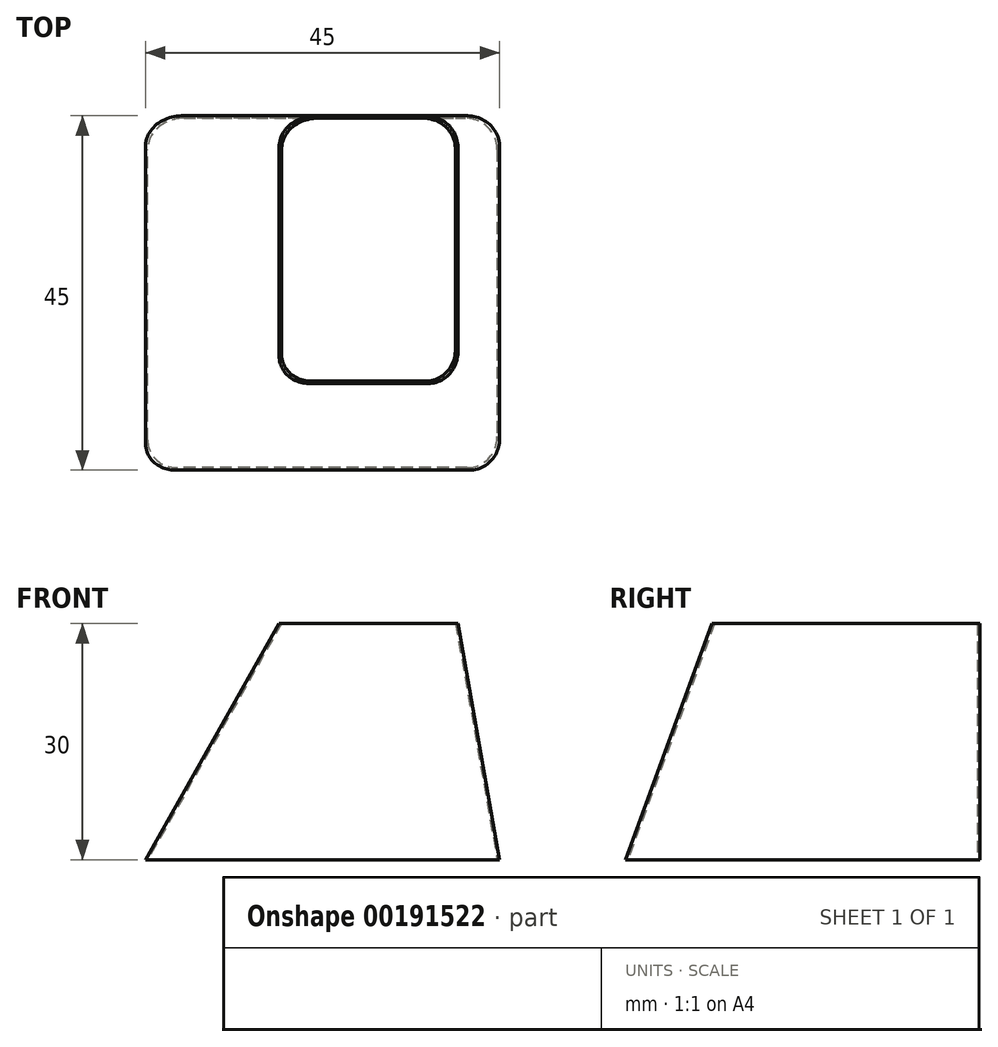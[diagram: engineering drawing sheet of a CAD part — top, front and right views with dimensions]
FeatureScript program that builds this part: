
annotation { "Feature Type Name" : "Feature", "Feature Type Description" : "" }
export const myFeature = defineFeature(function(context is Context, id is Id, definition is map)
    precondition{}
    {
        {
            var Q0;
            Q0=qCreatedBy(makeId("Top.planeOp"),FACE);
            var sketch = newSketch(context, id + "F0", { "sketchPlane" : qUnion([Q0])});
            skLineSegment(sketch, "E0.bottom", {"start": v(0, 0) * mm, "end": v(-45, 0) * mm});
            skLineSegment(sketch, "E0.top", {"start": v(0, 45) * mm, "end": v(-45, 45) * mm});
            skLineSegment(sketch, "E0.left", {"start": v(0, 0) * mm, "end": v(0, 45) * mm});
            skLineSegment(sketch, "E0.right", {"start": v(-45, 0) * mm, "end": v(-45, 45) * mm});
            skSolve(sketch);
        }
        {
            var Q0;
            Q0=qCreatedBy(makeId("Top.planeOp"),FACE);
            cPlane(context, id + "F1", {"entities" : qUnion([Q0]), "cplaneType" : CPlaneType.OFFSET, "offset" : 30 * mm, "width" : 150 * mm, "height" : 150 * mm});
        }
        {
            var Q0;
            Q0=qCreatedBy(id+"F1.planeOp",FACE);
            var sketch = newSketch(context, id + "F2", { "sketchPlane" : qUnion([Q0])});
            skLineSegment(sketch, "E1", {"start": v(0, 0) * mm, "end": v(-5.3, 0) * mm, "construction": true});
            skLineSegment(sketch, "E2", {"start": v(-5.3, 0) * mm, "end": v(-5.3, 11) * mm, "construction": true});
            skLineSegment(sketch, "E3.bottom", {"start": v(-5.3, 11) * mm, "end": v(-28, 11) * mm});
            skLineSegment(sketch, "E3.top", {"start": v(-5.3, 45) * mm, "end": v(-28, 45) * mm});
            skLineSegment(sketch, "E3.left", {"start": v(-5.3, 11) * mm, "end": v(-5.3, 45) * mm});
            skLineSegment(sketch, "E3.right", {"start": v(-28, 11) * mm, "end": v(-28, 45) * mm});
            skSolve(sketch);
        }
        {
            var Q0;
            Q0=makeQuery(id+"F2.imprint","IMPRINT",FACE,{"disambiguationData":[TD([[makeQuery(id+"F2.imprint","IMPRINT",EDGE,{"derivedFrom":sQuery(id+"F2.wireOp",EDGE,"E3.bottom")}),-1.0]])]});
            var Q1;
            Q1=makeQuery(id+"F0.imprint","IMPRINT",FACE,{"disambiguationData":[TD([[makeQuery(id+"F0.imprint","IMPRINT",EDGE,{"derivedFrom":sQuery(id+"F0.wireOp",EDGE,"E0.bottom")}),-1.0]])]});
            loft(context, id + "F3", {"sheetProfilesArray" : [{ "sheetProfileEntities" : qUnion([Q0]) }, { "sheetProfileEntities" : qUnion([Q1]) }]});
        }
        {
            var Q0;
            Q0=makeQuery(id+"F3.opLoft","CAP_FACE",FACE,{"disambiguationData":[OSD([makeQuery(id+"F2.imprint","IMPRINT",FACE,{"disambiguationData":[TD([[makeQuery(id+"F2.imprint","IMPRINT",EDGE,{"derivedFrom":sQuery(id+"F2.wireOp",EDGE,"E3.bottom")}),-1.0]])]})])],"isStart":true});
            var sketch = newSketch(context, id + "F4", { "sketchPlane" : qUnion([Q0])});
            skLineSegment(sketch, "E4.0", {"start": v(-27.7, 11.3) * mm, "end": v(-27.7, 44.7) * mm});
            skLineSegment(sketch, "E4.1", {"start": v(-5.6, 11.3) * mm, "end": v(-27.7, 11.3) * mm});
            skLineSegment(sketch, "E4.2", {"start": v(-5.6, 44.7) * mm, "end": v(-5.6, 11.3) * mm});
            skLineSegment(sketch, "E4.3", {"start": v(-27.7, 44.7) * mm, "end": v(-5.6, 44.7) * mm});
            skSolve(sketch);
        }
        {
            var Q0;
            Q0=makeQuery(id+"F3.opLoft","CAP_FACE",FACE,{"disambiguationData":[OSD([makeQuery(id+"F0.imprint","IMPRINT",FACE,{"disambiguationData":[TD([[makeQuery(id+"F0.imprint","IMPRINT",EDGE,{"derivedFrom":sQuery(id+"F0.wireOp",EDGE,"E0.bottom")}),-1.0]])]})])],"isStart":true});
            var sketch = newSketch(context, id + "F5", { "sketchPlane" : qUnion([Q0])});
            skLineSegment(sketch, "E5.0", {"start": v(-44.7, -0.3) * mm, "end": v(-44.7, -44.7) * mm});
            skLineSegment(sketch, "E5.1", {"start": v(-0.3, -0.3) * mm, "end": v(-44.7, -0.3) * mm});
            skLineSegment(sketch, "E5.2", {"start": v(-0.3, -44.7) * mm, "end": v(-0.3, -0.3) * mm});
            skLineSegment(sketch, "E5.3", {"start": v(-44.7, -44.7) * mm, "end": v(-0.3, -44.7) * mm});
            skSolve(sketch);
        }
        {
            var Q1;
            Q1 = qSketchRegion(id + "F4", true);
            var Q2;
            Q2 = qSketchRegion(id + "F5", true);
            loft(context, id + "F6", {"operationType" : NewBodyOperationType.REMOVE, "sheetProfilesArray" : [{ "sheetProfileEntities" : qUnion([Q1]) }, { "sheetProfileEntities" : qUnion([Q2]) }]});
        }
        {
            var Q0;
            Q0=makeQuery(id+"F6.boolean.opBoolean","COPY",EDGE,{"derivedFrom":makeQuery(id+"F6.opLoft","SWEPT_EDGE",EDGE,{"disambiguationData":[OSD([sQuery(id+"F4.wireOp",EDGE,"E4.0"),sQuery(id+"F4.wireOp",EDGE,"E4.3"),sQuery(id+"F5.wireOp",EDGE,"E5.0"),sQuery(id+"F5.wireOp",EDGE,"E5.3")])]})});
            var Q1;
            Q1=makeQuery(id+"F6.boolean.opBoolean","COPY",EDGE,{"derivedFrom":makeQuery(id+"F6.opLoft","SWEPT_EDGE",EDGE,{"disambiguationData":[OSD([sQuery(id+"F4.wireOp",EDGE,"E4.0"),sQuery(id+"F4.wireOp",EDGE,"E4.1"),sQuery(id+"F5.wireOp",EDGE,"E5.0"),sQuery(id+"F5.wireOp",EDGE,"E5.1")])]})});
            var Q2;
            Q2=makeQuery(id+"F6.boolean.opBoolean","COPY",EDGE,{"derivedFrom":makeQuery(id+"F6.opLoft","SWEPT_EDGE",EDGE,{"disambiguationData":[OSD([sQuery(id+"F4.wireOp",EDGE,"E4.1"),sQuery(id+"F4.wireOp",EDGE,"E4.2"),sQuery(id+"F5.wireOp",EDGE,"E5.1"),sQuery(id+"F5.wireOp",EDGE,"E5.2")])]})});
            var Q3;
            Q3=makeQuery(id+"F6.boolean.opBoolean","COPY",EDGE,{"derivedFrom":makeQuery(id+"F6.opLoft","SWEPT_EDGE",EDGE,{"disambiguationData":[OSD([sQuery(id+"F4.wireOp",EDGE,"E4.2"),sQuery(id+"F4.wireOp",EDGE,"E4.3"),sQuery(id+"F5.wireOp",EDGE,"E5.2"),sQuery(id+"F5.wireOp",EDGE,"E5.3")])]})});
            fillet(context, id + "F7", {"entities" : qUnion([Q0, Q1, Q2, Q3]), "radius" : 4 * mm, "tangentPropagation" : true, "allowEdgeOverflow" : false});
        }
        {
            var Q0;
            Q0=makeQuery(id+"F3.opLoft","SWEPT_EDGE",EDGE,{"disambiguationData":[OSD([sQuery(id+"F0.wireOp",EDGE,"E0.bottom"),sQuery(id+"F0.wireOp",EDGE,"E0.right"),sQuery(id+"F2.wireOp",EDGE,"E3.bottom"),sQuery(id+"F2.wireOp",EDGE,"E3.right")])]});
            var Q1;
            Q1=makeQuery(id+"F3.opLoft","SWEPT_EDGE",EDGE,{"disambiguationData":[OSD([sQuery(id+"F0.wireOp",EDGE,"E0.top"),sQuery(id+"F0.wireOp",EDGE,"E0.right"),sQuery(id+"F2.wireOp",EDGE,"E3.top"),sQuery(id+"F2.wireOp",EDGE,"E3.right")])]});
            var Q2;
            Q2=makeQuery(id+"F3.opLoft","SWEPT_EDGE",EDGE,{"disambiguationData":[OSD([sQuery(id+"F0.wireOp",EDGE,"E0.bottom"),sQuery(id+"F0.wireOp",EDGE,"E0.left"),sQuery(id+"F2.wireOp",EDGE,"E3.bottom"),sQuery(id+"F2.wireOp",EDGE,"E3.left")])]});
            var Q3;
            Q3=makeQuery(id+"F3.opLoft","SWEPT_EDGE",EDGE,{"disambiguationData":[OSD([sQuery(id+"F0.wireOp",EDGE,"E0.top"),sQuery(id+"F0.wireOp",EDGE,"E0.left"),sQuery(id+"F2.wireOp",EDGE,"E3.top"),sQuery(id+"F2.wireOp",EDGE,"E3.left")])]});
            fillet(context, id + "F8", {"entities" : qUnion([Q0, Q1, Q2, Q3]), "radius" : 4 * mm, "tangentPropagation" : true, "allowEdgeOverflow" : false});
        }
    });
